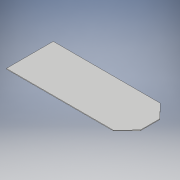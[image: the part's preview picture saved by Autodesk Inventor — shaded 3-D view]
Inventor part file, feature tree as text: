
AUTODESK INVENTOR PART (.ipt)
format: ipt  version: 2018 (Build 220112000, 112)  size: 99,840 bytes
history: native  units: in
note: dims shown in document units (in); Inventor stores cm internally (conversion verified against a paired STEP export)
features: extrude x1, sketch x1
ambient origin geometry x8: Origin, YZ Plane, XZ Plane, XY Plane, X Axis, Y Axis, Z Axis, Center Point
bodies: Solid1 (feature_tree)
feature tree (2):
  extrude  "Extrusion1"  Depth=0.031in TaperAngle=0.0deg
  sketch  "Sketch1"  dims[d1=2.1875in d4=0.031in d5=0.0in d6=5.0in d7=2.1875in d8=5.0in d9=0.9063in]
